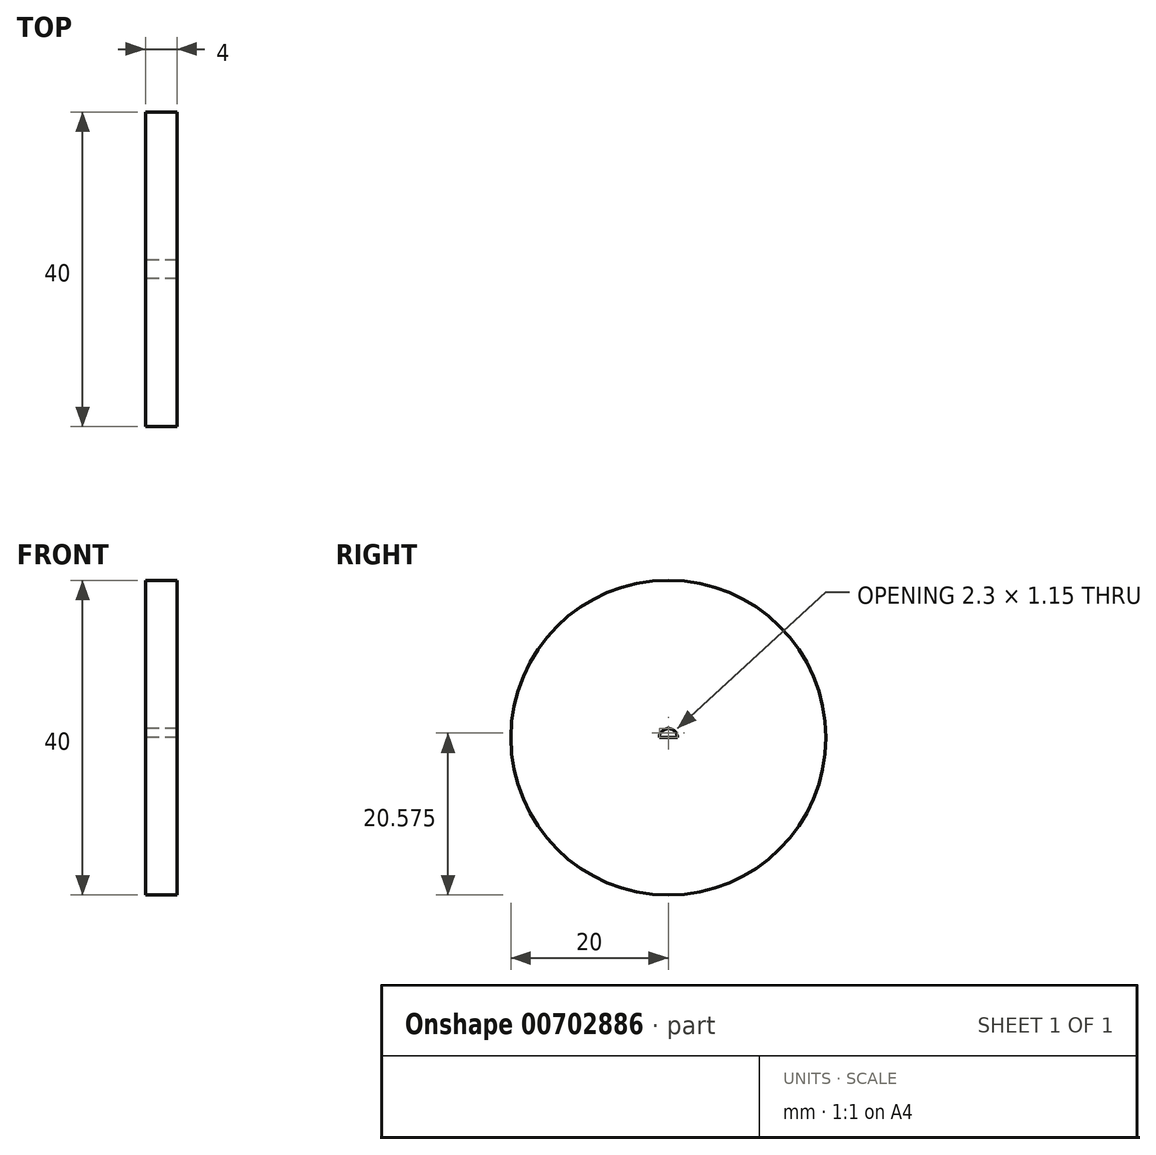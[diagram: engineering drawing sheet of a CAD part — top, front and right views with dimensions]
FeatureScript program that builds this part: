
annotation { "Feature Type Name" : "Feature", "Feature Type Description" : "" }
export const myFeature = defineFeature(function(context is Context, id is Id, definition is map)
    precondition{}
    {
        {
            var Q0;
            Q0=qCreatedBy(makeId("Right.planeOp"),FACE);
            var sketch = newSketch(context, id + "F0", { "sketchPlane" : qUnion([Q0])});
            skCircle(sketch, "E0", {"center": v(0, 0) * mm, "radius": 20 * mm});
            skArc(sketch, "E1", {"start": v(1.15, 0) * mm, "mid": v(0, 1.15) * mm, "end": v(-1.15, 0) * mm});
            skLineSegment(sketch, "E2", {"start": v(-1.15, 0) * mm, "end": v(1.15, 0) * mm});
            skSolve(sketch);
        }
        {
            var Q0;
            Q0 = qSketchRegion(id + "F0", true);
            extrude(context, id + "F1", {"entities" : qUnion([Q0]), "depth" : 4 * mm, "offsetDistance" : 25 * mm});
        }
    });
